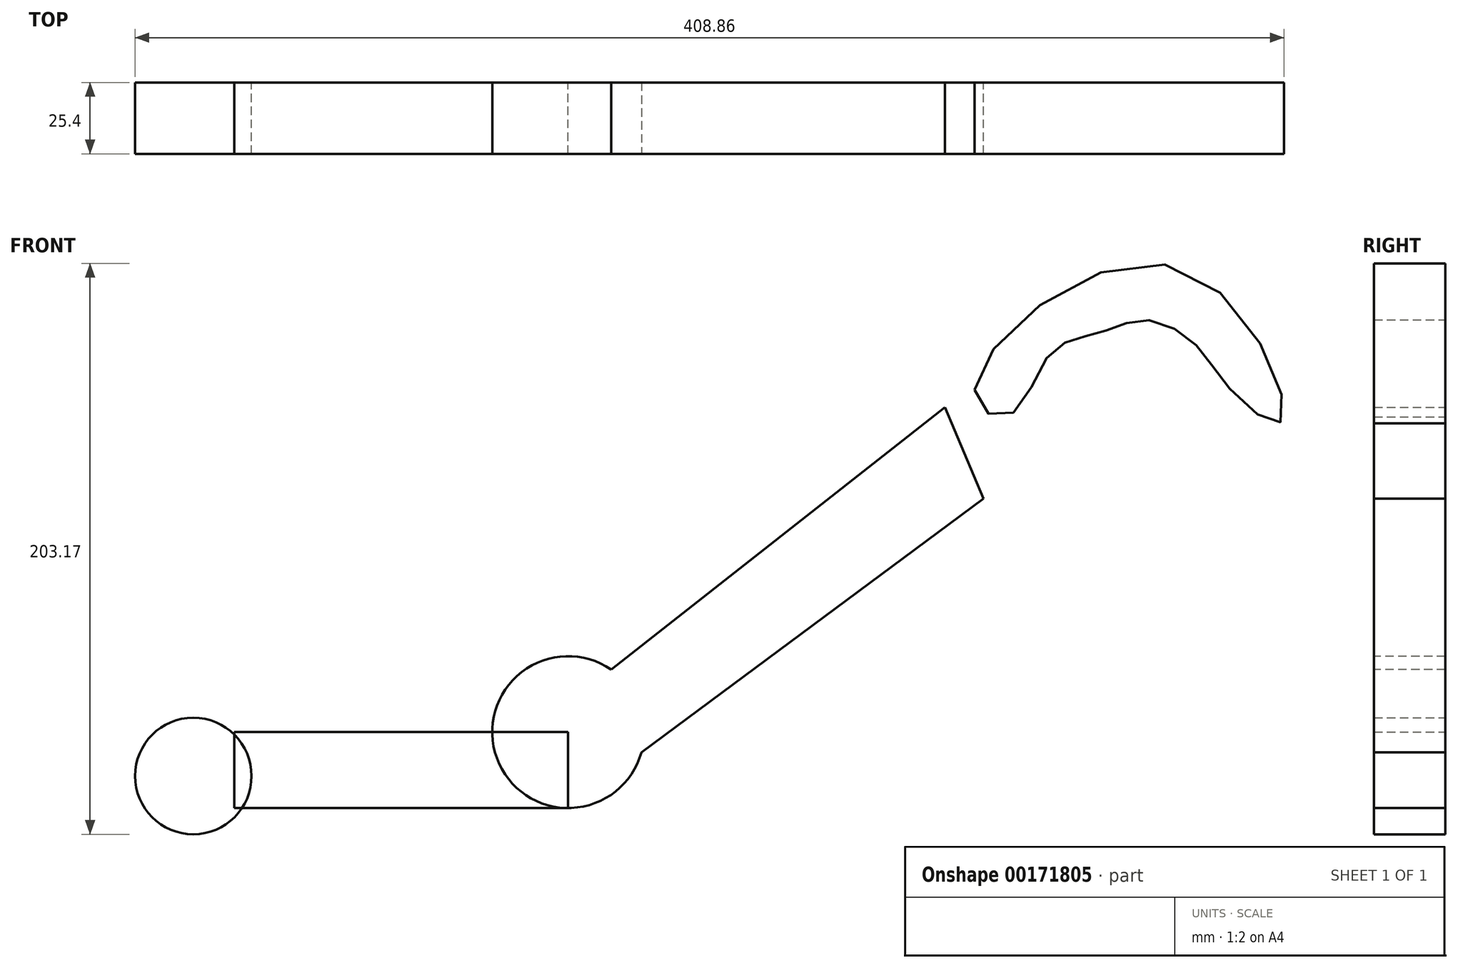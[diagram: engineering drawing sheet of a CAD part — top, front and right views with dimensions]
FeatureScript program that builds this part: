
annotation { "Feature Type Name" : "Feature", "Feature Type Description" : "" }
export const myFeature = defineFeature(function(context is Context, id is Id, definition is map)
    precondition{}
    {
        {
            var Q0;
            Q0=qCreatedBy(makeId("Front.planeOp"),FACE);
            var sketch = newSketch(context, id + "F0", { "sketchPlane" : qUnion([Q0])});
            skLineSegment(sketch, "E0.bottom", {"start": v(10.37, 69.83) * mm, "end": v(-10.37, 69.83) * mm});
            skLineSegment(sketch, "E0.top", {"start": v(10.37, -69.83) * mm, "end": v(-10.37, -69.83) * mm});
            skLineSegment(sketch, "E0.left", {"start": v(10.37, 69.83) * mm, "end": v(10.37, -69.83) * mm});
            skLineSegment(sketch, "E0.right", {"start": v(-10.37, 69.83) * mm, "end": v(-10.37, -69.83) * mm});
            skPoint(sketch, "E0.middle", {"position": v(0, 0) * mm});
            skSolve(sketch);
        }
        {
            var Q0;
            Q0=makeQuery(id+"F0.imprint","IMPRINT",FACE,{"disambiguationData":[TD([[makeQuery(id+"F0.imprint","IMPRINT",EDGE,{"derivedFrom":sQuery(id+"F0.wireOp",EDGE,"E0.bottom")}),1.0]])]});
            var Q1;
            Q1=sQuery(id+"F0.wireOp",EDGE,"E0.right");
            var Q2;
            Q2=sQuery(id+"F0.wireOp",EDGE,"E0.bottom");
            var Q3;
            Q3=sQuery(id+"F0.wireOp",EDGE,"E0.left");
            var Q4;
            Q4=sQuery(id+"F0.wireOp",EDGE,"E0.top");
            extrude(context, id + "F1", {"entities" : qUnion([Q0]), "bodyType" : ToolBodyType.SURFACE, "surfaceEntities" : qUnion([Q1, Q2, Q3, Q4]), "depth" : 25.4 * mm});
        }
        {
            var Q0;
            Q0=makeQuery(id+"F1.opExtrude","SWEPT_FACE",FACE,{"disambiguationData":[OSD([sQuery(id+"F0.wireOp",EDGE,"E0.bottom")])]});
            var Q1;
            Q1=makeQuery(id+"F1.opExtrude","SWEPT_EDGE",EDGE,{"disambiguationData":[OSD([sQuery(id+"F0.wireOp",VERTEX,"E0.left.start")])]});
            revolve(context, id + "F2", {"entities" : qUnion([Q0]), "axis" : qUnion([Q1]), "revolveType" : RevolveType.FULL});
        }
        {
            var Q0;
            Q0=qCreatedBy(makeId("Front.planeOp"),FACE);
            var sketch = newSketch(context, id + "F3", { "sketchPlane" : qUnion([Q0])});
            skLineSegment(sketch, "E1.bottom", {"start": v(24.96, 85.45) * mm, "end": v(143.75, 85.45) * mm});
            skLineSegment(sketch, "E1.top", {"start": v(24.96, 58.43) * mm, "end": v(143.75, 58.43) * mm});
            skLineSegment(sketch, "E1.left", {"start": v(24.96, 85.45) * mm, "end": v(24.96, 58.43) * mm});
            skLineSegment(sketch, "E1.right", {"start": v(143.75, 85.45) * mm, "end": v(143.75, 58.43) * mm});
            skSolve(sketch);
        }
        {
            var Q0;
            Q0=makeQuery(id+"F3.imprint","IMPRINT",FACE,{"disambiguationData":[TD([[makeQuery(id+"F3.imprint","IMPRINT",EDGE,{"derivedFrom":sQuery(id+"F3.wireOp",EDGE,"E1.bottom")}),-1.0]])]});
            extrude(context, id + "F4", {"entities" : qUnion([Q0]), "depth" : 25.4 * mm});
        }
        {
            var Q0;
            Q0=makeQuery(id+"F4.opExtrude","SWEPT_FACE",FACE,{"disambiguationData":[OSD([sQuery(id+"F3.wireOp",EDGE,"E1.right")])]});
            var Q1;
            Q1=makeQuery(id+"F4.opExtrude","SWEPT_EDGE",EDGE,{"disambiguationData":[OSD([sQuery(id+"F3.wireOp",EDGE,"E1.bottom"),sQuery(id+"F3.wireOp",EDGE,"E1.right")])]});
            revolve(context, id + "F5", {"entities" : qUnion([Q0]), "axis" : qUnion([Q1]), "revolveType" : RevolveType.FULL});
        }
        {
            var Q0;
            Q0=qCreatedBy(makeId("Front.planeOp"),FACE);
            var sketch = newSketch(context, id + "F6", { "sketchPlane" : qUnion([Q0])});
            skLineSegment(sketch, "E2", {"start": v(155.06, 104.54) * mm, "end": v(277.86, 201.01) * mm});
            skLineSegment(sketch, "E3", {"start": v(277.86, 201.01) * mm, "end": v(291.5, 168.57) * mm});
            skLineSegment(sketch, "E4", {"start": v(291.5, 168.57) * mm, "end": v(162.64, 73) * mm});
            skLineSegment(sketch, "E5", {"start": v(155.06, 104.54) * mm, "end": v(162.64, 73) * mm});
            skSolve(sketch);
        }
        {
            var Q0;
            Q0 = qSketchRegion(id + "F6", true);
            extrude(context, id + "F7", {"entities" : qUnion([Q0]), "operationType" : NewBodyOperationType.ADD, "depth" : 25.4 * mm});
        }
        {
            var Q0;
            Q0=qCreatedBy(makeId("Front.planeOp"),FACE);
            var sketch = newSketch(context, id + "F8", { "sketchPlane" : qUnion([Q0])});
            skFitSpline(sketch, "E6", {"points": [v(288.4, 207.33) * mm, v(359.81, 251.04) * mm, v(397.61, 196.15) * mm, v(378.71, 208.2) * mm, v(366.81, 223.66) * mm, v(350, 232.11) * mm, v(337.4, 229.17) * mm, v(325.5, 225.74) * mm, v(314.3, 219) * mm, v(300.3, 198.16) * mm, v(288.4, 207.33) * mm]});
            skSolve(sketch);
        }
        {
            var Q0;
            Q0 = qSketchRegion(id + "F8", true);
            extrude(context, id + "F9", {"entities" : qUnion([Q0]), "depth" : 25.4 * mm});
        }
    });
